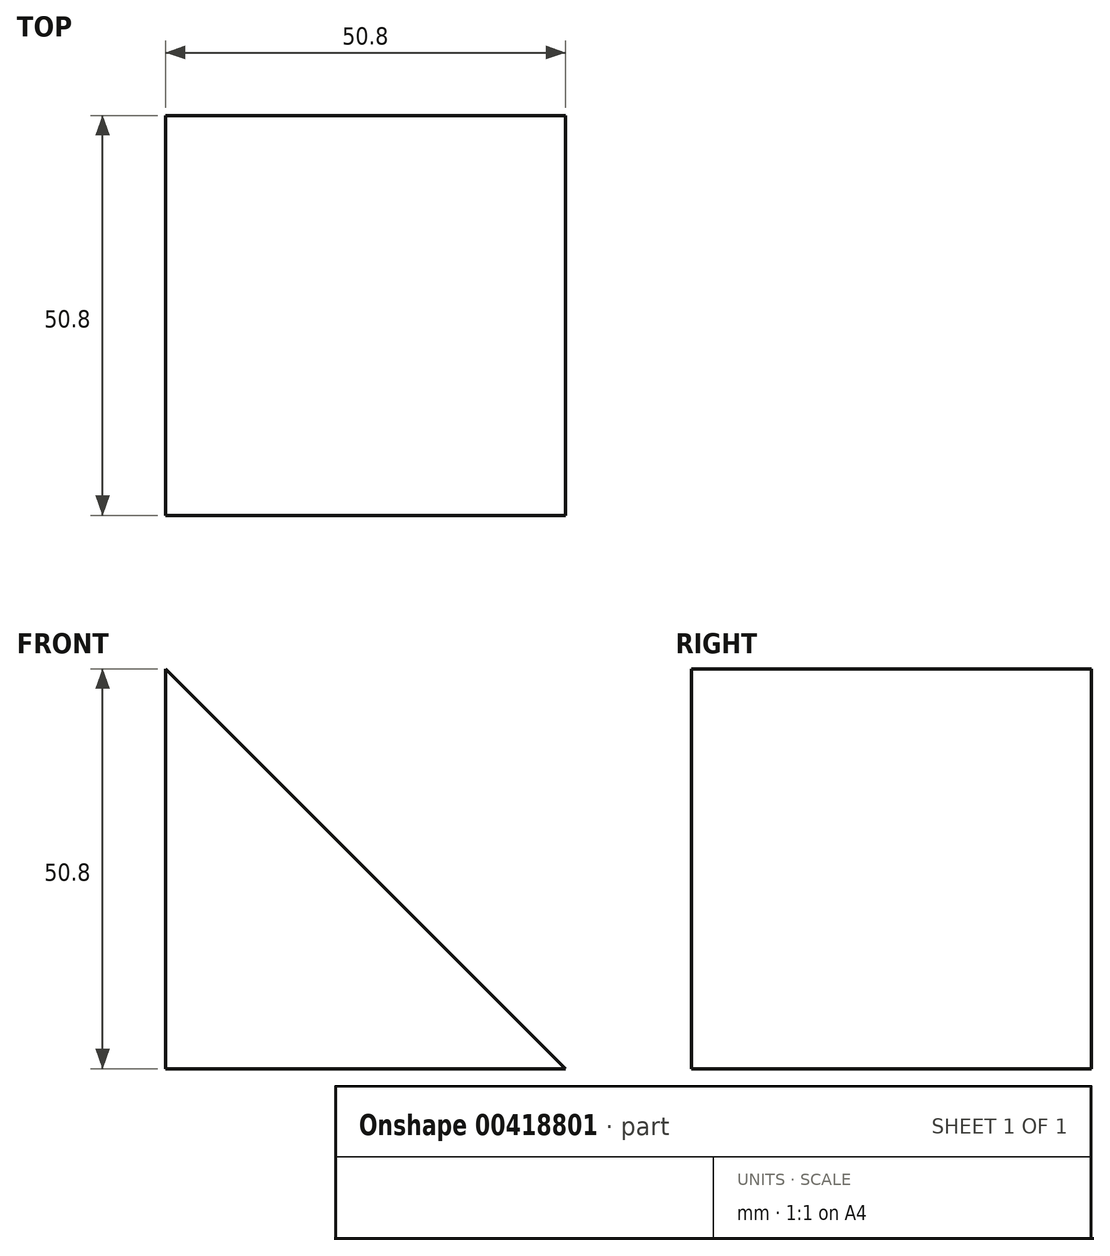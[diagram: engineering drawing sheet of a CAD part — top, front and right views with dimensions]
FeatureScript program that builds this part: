
annotation { "Feature Type Name" : "Feature", "Feature Type Description" : "" }
export const myFeature = defineFeature(function(context is Context, id is Id, definition is map)
    precondition{}
    {
        {
            var Q0;
            Q0=qCreatedBy(makeId("Front.planeOp"),FACE);
            var sketch = newSketch(context, id + "F0", { "sketchPlane" : qUnion([Q0])});
            skLineSegment(sketch, "E0", {"start": v(-50.8, 0) * mm, "end": v(-50.8, 50.8) * mm});
            skLineSegment(sketch, "E1", {"start": v(-50.8, 50.8) * mm, "end": v(0, 0) * mm});
            skLineSegment(sketch, "E2", {"start": v(0, 0) * mm, "end": v(-50.8, 0) * mm});
            skSolve(sketch);
        }
        {
            var Q0;
            Q0 = qSketchRegion(id + "F0", true);
            extrude(context, id + "F1", {"entities" : qUnion([Q0]), "depth" : 50.8 * mm});
        }
    });
